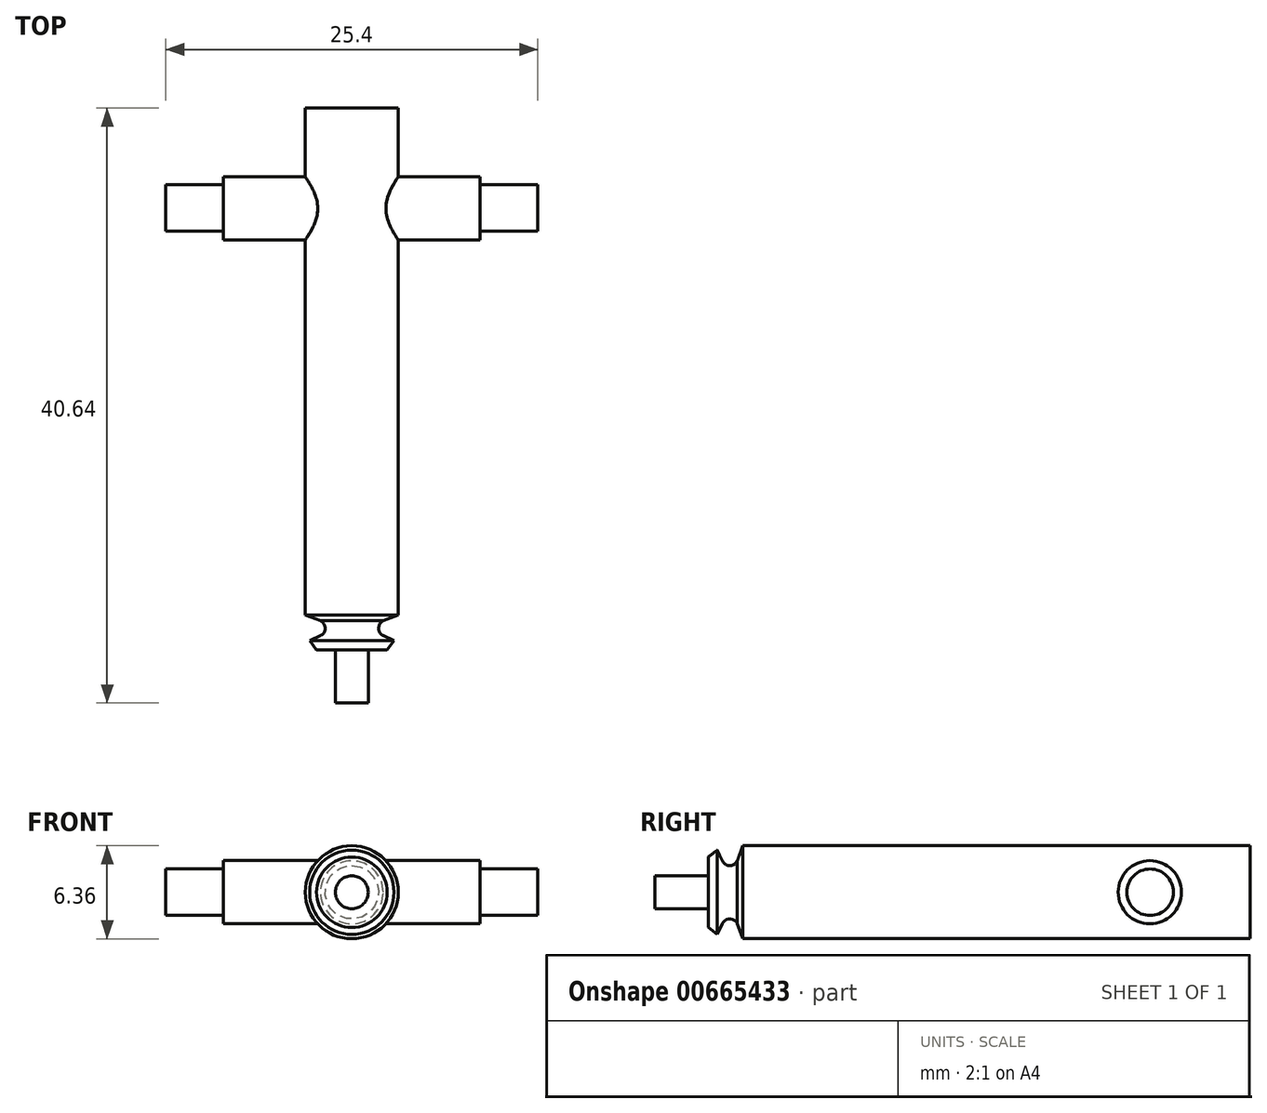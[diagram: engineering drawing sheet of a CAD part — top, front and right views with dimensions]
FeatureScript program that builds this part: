
annotation { "Feature Type Name" : "Feature", "Feature Type Description" : "" }
export const myFeature = defineFeature(function(context is Context, id is Id, definition is map)
    precondition{}
    {
        {
            var Q0;
            Q0=qCreatedBy(makeId("Front.planeOp"),FACE);
            var sketch = newSketch(context, id + "F0", { "sketchPlane" : qUnion([Q0])});
            skCircle(sketch, "E0", {"center": v(0, 0) * mm, "radius": 3.18 * mm});
            skSolve(sketch);
        }
        {
            var Q0;
            Q0 = qSketchRegion(id + "F0", true);
            var Q1;
            Q1 = qConstructionFilter(qBodyType(qCreatedBy(id + "F0" ,EDGE), BodyType.WIRE), ConstructionObject.NO);
            extrude(context, id + "F1", {"entities" : qUnion([Q0]), "surfaceEntities" : qUnion([Q1]), "depth" : 40.64 * mm, "offsetDistance" : 25.4 * mm});
        }
        {
            var Q0;
            Q0=qCreatedBy(makeId("Top.planeOp"),FACE);
            var sketch = newSketch(context, id + "F2", { "sketchPlane" : qUnion([Q0])});
            skLineSegment(sketch, "E1", {"start": v(2.48, -48.45) * mm, "end": v(3.7, -48.45) * mm});
            skLineSegment(sketch, "E2", {"start": v(3.7, -34.46) * mm, "end": v(3.7, -48.45) * mm});
            skLineSegment(sketch, "E3", {"start": v(3.7, -34.46) * mm, "end": v(2.15, -35.02) * mm});
            skLineSegment(sketch, "E4", {"start": v(2.15, -36.04) * mm, "end": v(2.88, -36.38) * mm});
            skLineSegment(sketch, "E5", {"start": v(2.88, -36.38) * mm, "end": v(2.4, -37) * mm});
            skLineSegment(sketch, "E6", {"start": v(2.4, -37) * mm, "end": v(1.12, -37) * mm});
            skLineSegment(sketch, "E7", {"start": v(1.12, -37) * mm, "end": v(1.12, -46.98) * mm});
            skArc(sketch, "E8", {"start": v(2.15, -35.02) * mm, "mid": v(1.82, -35.53) * mm, "end": v(2.15, -36.04) * mm});
            skLineSegment(sketch, "E9", {"start": v(2.48, -48.45) * mm, "end": v(2.48, -48.68) * mm});
            skLineSegment(sketch, "E10", {"start": v(1.12, -46.98) * mm, "end": v(2.48, -48.68) * mm});
            skLineSegment(sketch, "E11", {"start": v(0, -50.7) * mm, "end": v(0, -39.67) * mm});
            skSolve(sketch);
        }
        {
            var Q0;
            Q0=makeQuery(id+"F2.imprint","IMPRINT",FACE,{"disambiguationData":[TD([[makeQuery(id+"F2.imprint","IMPRINT",EDGE,{"derivedFrom":sQuery(id+"F2.wireOp",EDGE,"E1")}),1.0]])]});
            var Q1;
            Q1=sQuery(id+"F2.wireOp",EDGE,"E11");
            revolve(context, id + "F3", {"operationType" : NewBodyOperationType.REMOVE, "entities" : qUnion([Q0]), "axis" : qUnion([Q1]), "revolveType" : RevolveType.FULL, "oppositeDirection" : true});
        }
        {
            var Q0;
            Q0=qCreatedBy(makeId("Right.planeOp"),FACE);
            var sketch = newSketch(context, id + "F4", { "sketchPlane" : qUnion([Q0])});
            skCircle(sketch, "E12", {"center": v(-6.85, 0) * mm, "radius": 2.16 * mm});
            skSolve(sketch);
        }
        {
            var Q0;
            Q0 = qSketchRegion(id + "F4", true);
            extrude(context, id + "F5", {"entities" : qUnion([Q0]), "operationType" : NewBodyOperationType.ADD, "depth" : 17.53 * mm, "offsetDistance" : 25.4 * mm, "symmetric" : true});
        }
        {
            var Q0;
            Q0=qCreatedBy(makeId("Right.planeOp"),FACE);
            var sketch = newSketch(context, id + "F6", { "sketchPlane" : qUnion([Q0])});
            skCircle(sketch, "E13", {"center": v(-6.83, 0) * mm, "radius": 1.59 * mm});
            skSolve(sketch);
        }
        {
            var Q0;
            Q0 = qSketchRegion(id + "F6", true);
            extrude(context, id + "F7", {"entities" : qUnion([Q0]), "operationType" : NewBodyOperationType.ADD, "depth" : 25.4 * mm, "offsetDistance" : 25.4 * mm, "symmetric" : true});
        }
    });
